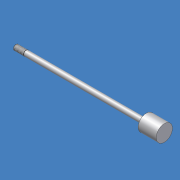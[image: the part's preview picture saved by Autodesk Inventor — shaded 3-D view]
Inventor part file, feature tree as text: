
AUTODESK INVENTOR PART (.ipt)
format: ipt  version: 2012 (Build 160160000, 160)  size: 125,952 bytes
history: native  units: mm (DEFAULTED — no unit token found)
features: other x84, revolve x3, sketch x3, thread x1
ambient origin geometry x8: Origin, YZ Plane, XZ Plane, XY Plane, X Axis, Y Axis, Z Axis, Center Point
bodies: Solid1 (feature_tree)
feature tree (91):
  revolve  "Revolution1"  Angle=360.0deg
  revolve  "Revolution2"  Angle=360.0deg
  thread  "Thread1"  [1 undecoded]
  revolve  "Revolution3"  [1 undecoded]
  other  "rod_cp_XY"
  other  "rod_cp_YZ"
  other  "rod_cp_ZX"
  other  "rod_cp_X"
  other  "rod_cp_Y"
  other  "rod_cp_Z"
  other  "rod_cp_Center"
  other  "to_rod_clevis_XY"
  other  "to_rod_clevis_YZ"
  other  "to_rod_clevis_ZX"
  other  "to_rod_clevis_X"
  other  "to_rod_clevis_Y"
  other  "to_rod_clevis_Z"
  other  "to_rod_clevis_Center"
  other  "rl2_XY"
  other  "rl2_YZ"
  other  "rl2_ZX"
  other  "rl2_X"
  other  "rl2_Y"
  other  "rl2_Z"
  other  "rl2_Center"
  other  "rl1_XY"
  other  "rl1_YZ"
  other  "rl1_ZX"
  other  "rl1_X"
  other  "rl1_Y"
  other  "rl1_Z"
  other  "rl1_Center"
  other  "thd1_XY"
  other  "thd1_YZ"
  other  "thd1_ZX"
  other  "thd1_X"
  other  "thd1_Y"
  other  "thd1_Z"
  other  "thd1_Center"
  other  "thd2_XY"
  other  "thd2_YZ"
  other  "thd2_ZX"
  other  "thd2_X"
  other  "thd2_Y"
  other  "thd2_Z"
  other  "thd2_Center"
  other  "dia1_XY"
  other  "dia1_YZ"
  other  "dia1_ZX"
  other  "dia1_X"
  other  "dia1_Y"
  other  "dia1_Z"
  other  "dia1_Center"
  other  "dia2_XY"
  other  "dia2_YZ"
  other  "dia2_ZX"
  other  "dia2_X"
  other  "dia2_Y"
  other  "dia2_Z"
  other  "dia2_Center"
  other  "hh1_XY"
  other  "hh1_YZ"
  other  "hh1_ZX"
  other  "hh1_X"
  other  "hh1_Y"
  other  "hh1_Z"
  other  "hh1_Center"
  other  "hh2_XY"
  other  "hh2_YZ"
  other  "hh2_ZX"
  other  "hh2_X"
  other  "hh2_Y"
  other  "hh2_Z"
  other  "hh2_Center"
  other  "dia12_XY"
  other  "dia12_YZ"
  other  "dia12_ZX"
  other  "dia12_X"
  other  "dia12_Y"
  other  "dia12_Z"
  other  "dia12_Center"
  other  "dia22_XY"
  other  "dia22_YZ"
  other  "dia22_ZX"
  other  "dia22_X"
  other  "dia22_Y"
  other  "dia22_Z"
  other  "dia22_Center"
  sketch  "Sketch_1"  dims[d0=360.0deg d1=360.0deg]
  sketch  "Sketch_3"  dims[d2=12.7mm d3=142.0876mm d4=360.0deg]
  sketch  "Sketch_30"
note: 2 required parameter values undecoded (feature->parameter linkage not recoverable at this tier; creation-order binding heuristic only, values carry confidence <= 0.55)
